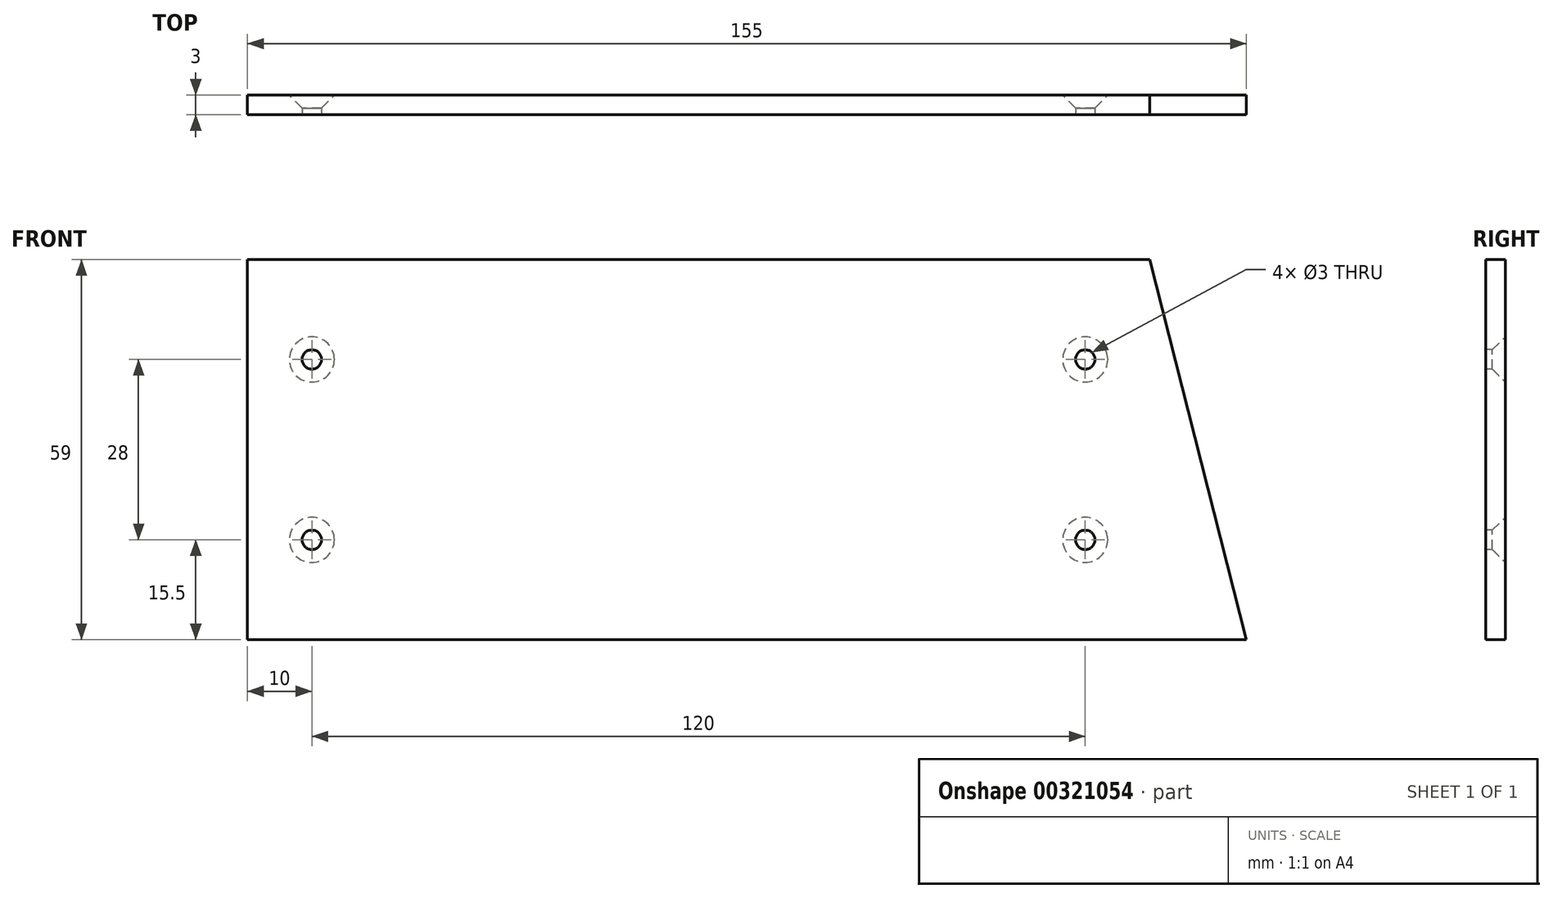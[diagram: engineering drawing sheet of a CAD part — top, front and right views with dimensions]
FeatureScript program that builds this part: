
annotation { "Feature Type Name" : "Feature", "Feature Type Description" : "" }
export const myFeature = defineFeature(function(context is Context, id is Id, definition is map)
    precondition{}
    {
        {
            var Q0;
            Q0=qCreatedBy(makeId("Front.planeOp"),FACE);
            var sketch = newSketch(context, id + "F0", { "sketchPlane" : qUnion([Q0])});
            skLineSegment(sketch, "E0.bottom", {"start": v(70, 29.5) * mm, "end": v(-70, 29.5) * mm});
            skLineSegment(sketch, "E0.top", {"start": v(70, -29.5) * mm, "end": v(-70, -29.5) * mm});
            skLineSegment(sketch, "E0.left", {"start": v(70, 29.5) * mm, "end": v(70, -29.5) * mm});
            skLineSegment(sketch, "E0.right", {"start": v(-70, 29.5) * mm, "end": v(-70, -29.5) * mm});
            skPoint(sketch, "E0.middle", {"position": v(0, 0) * mm});
            skLineSegment(sketch, "E1", {"start": v(70, 29.5) * mm, "end": v(85, -29.5) * mm});
            skLineSegment(sketch, "E2", {"start": v(85, -29.5) * mm, "end": v(70, -29.5) * mm});
            skSolve(sketch);
        }
        {
            var Q0;
            Q0=qSketchRegion(id+"F0",true);
            extrude(context, id + "F1", {"entities" : qUnion([Q0]), "depth" : 3 * mm});
        }
        {
            var Q0;
            Q0=makeQuery(id+"F1.opExtrude","CAP_FACE",FACE,{"disambiguationData":[OSD([sQuery(id+"F0.wireOp",EDGE,"E0.bottom"),sQuery(id+"F0.wireOp",EDGE,"E0.top"),sQuery(id+"F0.wireOp",EDGE,"E0.right"),sQuery(id+"F0.wireOp",EDGE,"E1"),sQuery(id+"F0.wireOp",EDGE,"E2")])],"isStart":false});
            var sketch = newSketch(context, id + "F2", { "sketchPlane" : qUnion([Q0])});
            skCircle(sketch, "E3", {"center": v(-60, 14) * mm, "radius": 1.5 * mm});
            skCircle(sketch, "E4", {"center": v(60, 14) * mm, "radius": 1.5 * mm});
            skCircle(sketch, "E5", {"center": v(60, -14) * mm, "radius": 1.5 * mm});
            skCircle(sketch, "E6", {"center": v(-60, -14) * mm, "radius": 1.5 * mm});
            skSolve(sketch);
        }
        {
            var Q0;
            Q0 = qSketchRegion(id + "F2", true);
            extrude(context, id + "F3", {"entities" : qUnion([Q0]), "operationType" : NewBodyOperationType.REMOVE, "oppositeDirection" : true, "depth" : 25 * mm});
        }
        {
            var Q0;
            Q0=makeQuery(id+"F3.boolean.opBoolean","INTERSECT",EDGE,{"derivedFrom":[makeQuery(id+"F1.opExtrude","CAP_FACE",FACE,{"disambiguationData":[OSD([sQuery(id+"F0.wireOp",EDGE,"E0.bottom"),sQuery(id+"F0.wireOp",EDGE,"E0.top"),sQuery(id+"F0.wireOp",EDGE,"E0.right"),sQuery(id+"F0.wireOp",EDGE,"E1"),sQuery(id+"F0.wireOp",EDGE,"E2")])],"isStart":true}),makeQuery(id+"F3.opExtrude","SWEPT_FACE",FACE,{"disambiguationData":[OSD([sQuery(id+"F2.wireOp",EDGE,"E6")])]})]});
            var Q1;
            Q1=makeQuery(id+"F3.boolean.opBoolean","INTERSECT",EDGE,{"derivedFrom":[makeQuery(id+"F1.opExtrude","CAP_FACE",FACE,{"disambiguationData":[OSD([sQuery(id+"F0.wireOp",EDGE,"E0.bottom"),sQuery(id+"F0.wireOp",EDGE,"E0.top"),sQuery(id+"F0.wireOp",EDGE,"E0.right"),sQuery(id+"F0.wireOp",EDGE,"E1"),sQuery(id+"F0.wireOp",EDGE,"E2")])],"isStart":true}),makeQuery(id+"F3.opExtrude","SWEPT_FACE",FACE,{"disambiguationData":[OSD([sQuery(id+"F2.wireOp",EDGE,"E3")])]})]});
            var Q2;
            Q2=makeQuery(id+"F3.boolean.opBoolean","INTERSECT",EDGE,{"derivedFrom":[makeQuery(id+"F1.opExtrude","CAP_FACE",FACE,{"disambiguationData":[OSD([sQuery(id+"F0.wireOp",EDGE,"E0.bottom"),sQuery(id+"F0.wireOp",EDGE,"E0.top"),sQuery(id+"F0.wireOp",EDGE,"E0.right"),sQuery(id+"F0.wireOp",EDGE,"E1"),sQuery(id+"F0.wireOp",EDGE,"E2")])],"isStart":true}),makeQuery(id+"F3.opExtrude","SWEPT_FACE",FACE,{"disambiguationData":[OSD([sQuery(id+"F2.wireOp",EDGE,"E5")])]})]});
            var Q3;
            Q3=makeQuery(id+"F3.boolean.opBoolean","INTERSECT",EDGE,{"derivedFrom":[makeQuery(id+"F1.opExtrude","CAP_FACE",FACE,{"disambiguationData":[OSD([sQuery(id+"F0.wireOp",EDGE,"E0.bottom"),sQuery(id+"F0.wireOp",EDGE,"E0.top"),sQuery(id+"F0.wireOp",EDGE,"E0.right"),sQuery(id+"F0.wireOp",EDGE,"E1"),sQuery(id+"F0.wireOp",EDGE,"E2")])],"isStart":true}),makeQuery(id+"F3.opExtrude","SWEPT_FACE",FACE,{"disambiguationData":[OSD([sQuery(id+"F2.wireOp",EDGE,"E4")])]})]});
            chamfer(context, id + "F4", {"entities" : qUnion([Q0, Q1, Q2, Q3]), "width" : 2 * mm, "tangentPropagation" : true});
        }
    });
